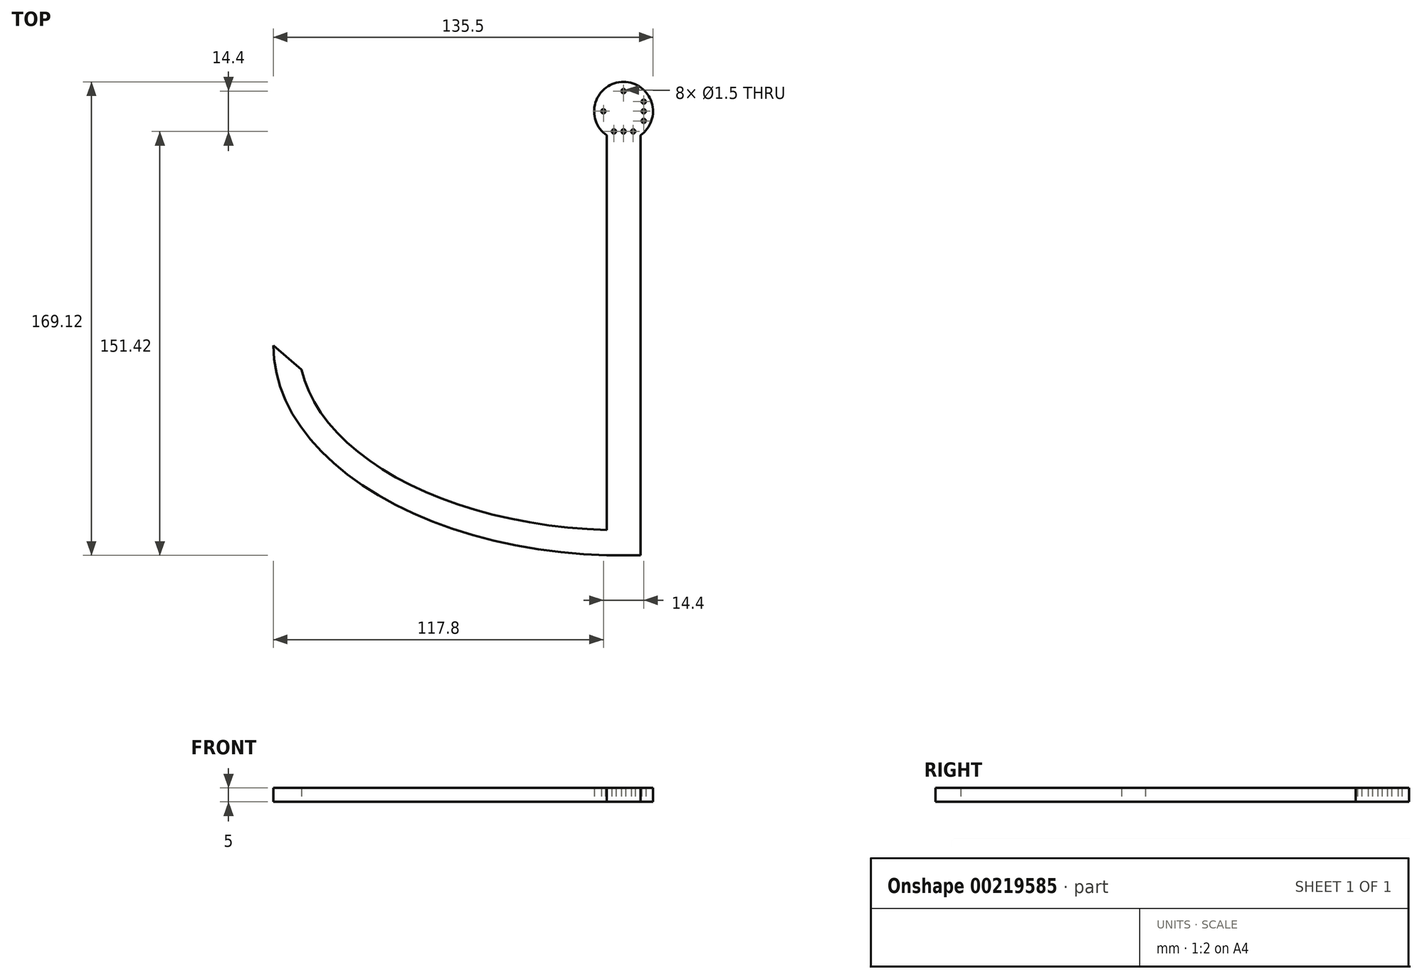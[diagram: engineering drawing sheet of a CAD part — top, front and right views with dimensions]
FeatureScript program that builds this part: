
annotation { "Feature Type Name" : "Feature", "Feature Type Description" : "" }
export const myFeature = defineFeature(function(context is Context, id is Id, definition is map)
    precondition{}
    {
        {
            var Q0;
            Q0=qCreatedBy(makeId("Top.planeOp"),FACE);
            var sketch = newSketch(context, id + "F0", { "sketchPlane" : qUnion([Q0])});
            skCircle(sketch, "E0", {"center": v(0, 0) * mm, "radius": 10.5 * mm});
            skCircle(sketch, "E1", {"center": v(0, 7.2) * mm, "radius": 0.75 * mm});
            skCircle(sketch, "E2", {"center": v(3.45, 7.2) * mm, "radius": 0.75 * mm});
            skCircle(sketch, "E3", {"center": v(-3.45, 7.2) * mm, "radius": 0.75 * mm});
            skLineSegment(sketch, "E4", {"start": v(-3.45, 7.2) * mm, "end": v(0, 7.2) * mm, "construction": true});
            skLineSegment(sketch, "E5", {"start": v(0, 7.2) * mm, "end": v(3.45, 7.2) * mm, "construction": true});
            skLineSegment(sketch, "E6", {"start": v(0, 0) * mm, "end": v(8.99, 8.99) * mm, "construction": true});
            skCircle(sketch, "E7.MirrorC", {"center": v(7.2, 3.45) * mm, "radius": 0.75 * mm});
            skCircle(sketch, "E8.MirrorC", {"center": v(7.2, 0) * mm, "radius": 0.75 * mm});
            skCircle(sketch, "E9.MirrorC", {"center": v(7.2, -3.45) * mm, "radius": 0.75 * mm});
            skCircle(sketch, "E10.MirrorC", {"center": v(-7.2, 3.45) * mm, "radius": 0.75 * mm});
            skCircle(sketch, "E11.MirrorC", {"center": v(-7.2, 0) * mm, "radius": 0.75 * mm});
            skCircle(sketch, "E12.MirrorC", {"center": v(-7.2, -3.45) * mm, "radius": 0.75 * mm});
            skCircle(sketch, "E13.MirrorC", {"center": v(-3.45, -7.2) * mm, "radius": 0.75 * mm});
            skCircle(sketch, "E14.MirrorC", {"center": v(0, -7.2) * mm, "radius": 0.75 * mm});
            skCircle(sketch, "E15.MirrorC", {"center": v(3.45, -7.2) * mm, "radius": 0.75 * mm});
            skSolve(sketch);
        }
        {
            var Q0;
            Q0=makeQuery(id+"F0.imprint","IMPRINT",FACE,{"disambiguationData":[TD([[makeQuery(id+"F0.imprint","IMPRINT",EDGE,{"derivedFrom":sQuery(id+"F0.wireOp",EDGE,"E15.MirrorC")}),-1.0]])]});
            var Q1;
            Q1=makeQuery(id+"F0.imprint","IMPRINT",FACE,{"disambiguationData":[TD([[makeQuery(id+"F0.imprint","IMPRINT",EDGE,{"derivedFrom":sQuery(id+"F0.wireOp",EDGE,"E13.MirrorC")}),-1.0]])]});
            var Q2;
            Q2=makeQuery(id+"F0.imprint","IMPRINT",FACE,{"disambiguationData":[TD([[makeQuery(id+"F0.imprint","IMPRINT",EDGE,{"derivedFrom":sQuery(id+"F0.wireOp",EDGE,"E12.MirrorC")}),1.0]])]});
            var Q3;
            Q3=makeQuery(id+"F0.imprint","IMPRINT",FACE,{"disambiguationData":[TD([[makeQuery(id+"F0.imprint","IMPRINT",EDGE,{"derivedFrom":sQuery(id+"F0.wireOp",EDGE,"E0")}),1.0]])]});
            var Q4;
            Q4=makeQuery(id+"F0.imprint","IMPRINT",FACE,{"disambiguationData":[TD([[makeQuery(id+"F0.imprint","IMPRINT",EDGE,{"derivedFrom":sQuery(id+"F0.wireOp",EDGE,"E10.MirrorC")}),1.0]])]});
            var Q5;
            Q5=makeQuery(id+"F0.imprint","IMPRINT",FACE,{"disambiguationData":[TD([[makeQuery(id+"F0.imprint","IMPRINT",EDGE,{"derivedFrom":sQuery(id+"F0.wireOp",EDGE,"E3")}),1.0]])]});
            var Q6;
            Q6=makeQuery(id+"F0.imprint","IMPRINT",FACE,{"disambiguationData":[TD([[makeQuery(id+"F0.imprint","IMPRINT",EDGE,{"derivedFrom":sQuery(id+"F0.wireOp",EDGE,"E2")}),1.0]])]});
            var Q7;
            Q7=makeQuery(id+"F0.imprint","IMPRINT",FACE,{"disambiguationData":[TD([[makeQuery(id+"F0.imprint","IMPRINT",EDGE,{"derivedFrom":sQuery(id+"F0.wireOp",EDGE,"E7.MirrorC")}),-1.0]])]});
            var Q8;
            Q8=makeQuery(id+"F0.imprint","IMPRINT",FACE,{"disambiguationData":[TD([[makeQuery(id+"F0.imprint","IMPRINT",EDGE,{"derivedFrom":sQuery(id+"F0.wireOp",EDGE,"E9.MirrorC")}),-1.0]])]});
            extrude(context, id + "F1", {"entities" : qUnion([Q0, Q1, Q2, Q3, Q4, Q5, Q6, Q7, Q8]), "depth" : 5 * mm});
        }
        {
            var Q0;
            Q0=qCreatedBy(makeId("Top.planeOp"),FACE);
            var sketch = newSketch(context, id + "F2", { "sketchPlane" : qUnion([Q0])});
            skLineSegment(sketch, "E16.bottom", {"start": v(6, -8.62) * mm, "end": v(-6, -8.62) * mm});
            skLineSegment(sketch, "E16.top", {"start": v(6, -158.62) * mm, "end": v(-6, -158.62) * mm});
            skLineSegment(sketch, "E16.left", {"start": v(6, -8.62) * mm, "end": v(6, -158.62) * mm});
            skLineSegment(sketch, "E16.right", {"start": v(-6, -8.62) * mm, "end": v(-6, -158.62) * mm});
            skPoint(sketch, "E16.middle", {"position": v(0, -83.62) * mm});
            skEllipse(sketch, "E17", {"center": v(0, -83.62) * mm, "majorRadius": 125 * mm, "minorRadius": 75 * mm, "majorAxis": v(-1, 0)});
            skEllipse(sketch, "E18", {"center": v(0, -83.62) * mm, "majorRadius": 116 * mm, "minorRadius": 66 * mm, "majorAxis": v(-1, 0)});
            skLineSegment(sketch, "E19", {"start": v(-115.01, -92.22) * mm, "end": v(-125, -83.62) * mm});
            skSolve(sketch);
        }
        {
            var Q0;
            {var subQ0=sQuery(id+"F2.wireOp",EDGE,"E16.bottom");Q0=makeQuery(id+"F2.imprint","IMPRINT",FACE,{"disambiguationData":[TD([[makeQuery(id+"F2.imprint","IMPRINT",EDGE,{"derivedFrom":subQ0}),1.0]])]});}
            var Q1;
            {var subQ0=sQuery(id+"F2.wireOp",EDGE,"E16.left");var subQ1=sQuery(id+"F2.wireOp",EDGE,"E16.top");var subQ2=makeQuery(id+"F2.imprint","INTERSECT",VERTEX,{"derivedFrom":[subQ1,subQ0]});Q1=makeQuery(id+"F2.imprint","IMPRINT",FACE,{"disambiguationData":[TD([[makeQuery(id+"F2.imprint","IMPRINT",EDGE,{"disambiguationData":[TD([[subQ2,-1.0]])],"derivedFrom":subQ1}),-1.0]])]});}
            var Q2;
            {var subQ0=sQuery(id+"F2.wireOp",EDGE,"E16.right");var subQ1=sQuery(id+"F2.wireOp",EDGE,"E16.top");var subQ2=makeQuery(id+"F2.imprint","INTERSECT",VERTEX,{"derivedFrom":[subQ1,subQ0]});Q2=makeQuery(id+"F2.imprint","IMPRINT",FACE,{"disambiguationData":[TD([[makeQuery(id+"F2.imprint","IMPRINT",EDGE,{"disambiguationData":[TD([[subQ2,1.0]])],"derivedFrom":subQ1}),-1.0]])]});}
            var Q3;
            {var subQ5=sQuery(id+"F2.wireOp",EDGE,"nrAR1SZ8-eQOA-jfP7-UnbU-oCX0eAFFnT3R");Q3=makeQuery(id+"F2.imprint","IMPRINT",FACE,{"disambiguationData":[TD([[makeQuery(id+"F2.imprint","IMPRINT",EDGE,{"derivedFrom":subQ5}),1.0]])]});}
            var Q4;
            {var subQ0=sQuery(id+"F2.wireOp",EDGE,"E17");var subQ2=sQuery(id+"F2.wireOp",EDGE,"E16.left");var subQ3=makeQuery(id+"F2.imprint","INTERSECT",VERTEX,{"disambiguationData":[OD(1.0)],"derivedFrom":[subQ2,subQ0]});Q4=makeQuery(id+"F2.imprint","IMPRINT",FACE,{"disambiguationData":[TD([[makeQuery(id+"F2.imprint","IMPRINT",EDGE,{"disambiguationData":[TD([[subQ3,1.0]])],"derivedFrom":subQ2}),-1.0]])]});}
            var Q5;
            {var subQ0=sQuery(id+"F2.wireOp",EDGE,"E17");var subQ1=sQuery(id+"F2.wireOp",EDGE,"E16.left");var subQ2=makeQuery(id+"F2.imprint","INTERSECT",VERTEX,{"disambiguationData":[OD(0.0)],"derivedFrom":[subQ1,subQ0]});Q5=makeQuery(id+"F2.imprint","IMPRINT",FACE,{"disambiguationData":[TD([[makeQuery(id+"F2.imprint","IMPRINT",EDGE,{"disambiguationData":[TD([[subQ2,-1.0]])],"derivedFrom":subQ1}),-1.0]])]});}
            var Q6;
            {var subQ0=sQuery(id+"F2.wireOp",EDGE,"E18");var subQ1=sQuery(id+"F2.wireOp",EDGE,"E16.left");var subQ2=makeQuery(id+"F2.imprint","INTERSECT",VERTEX,{"disambiguationData":[OD(0.0)],"derivedFrom":[subQ1,subQ0]});Q6=makeQuery(id+"F2.imprint","IMPRINT",FACE,{"disambiguationData":[TD([[makeQuery(id+"F2.imprint","IMPRINT",EDGE,{"disambiguationData":[TD([[subQ2,-1.0]])],"derivedFrom":subQ1}),-1.0]])]});}
            var Q7;
            {var subQ5=sQuery(id+"F2.wireOp",EDGE,"E19");Q7=makeQuery(id+"F2.imprint","IMPRINT",FACE,{"disambiguationData":[TD([[makeQuery(id+"F2.imprint","IMPRINT",EDGE,{"derivedFrom":subQ5}),1.0]])]});}
            var Q8;
            Q8=makeQuery(id+"F1.opExtrude","CAP_FACE",FACE,{"disambiguationData":[OSD([sQuery(id+"F0.wireOp",EDGE,"E0"),sQuery(id+"F0.wireOp",EDGE,"E1"),sQuery(id+"F0.wireOp",EDGE,"E2"),sQuery(id+"F0.wireOp",EDGE,"E3"),sQuery(id+"F0.wireOp",EDGE,"E7.MirrorC"),sQuery(id+"F0.wireOp",EDGE,"E8.MirrorC"),sQuery(id+"F0.wireOp",EDGE,"E9.MirrorC"),sQuery(id+"F0.wireOp",EDGE,"E10.MirrorC"),sQuery(id+"F0.wireOp",EDGE,"E11.MirrorC"),sQuery(id+"F0.wireOp",EDGE,"E12.MirrorC"),sQuery(id+"F0.wireOp",EDGE,"E13.MirrorC"),sQuery(id+"F0.wireOp",EDGE,"E14.MirrorC"),sQuery(id+"F0.wireOp",EDGE,"E15.MirrorC")])],"isStart":false});
            extrude(context, id + "F3", {"entities" : qUnion([Q0, Q1, Q2, Q3, Q4, Q5, Q6, Q7]), "operationType" : NewBodyOperationType.ADD, "endBound" : BoundingType.UP_TO_SURFACE, "endBoundEntityFace" : qUnion([Q8]), "depth" : 25 * mm});
        }
    });
